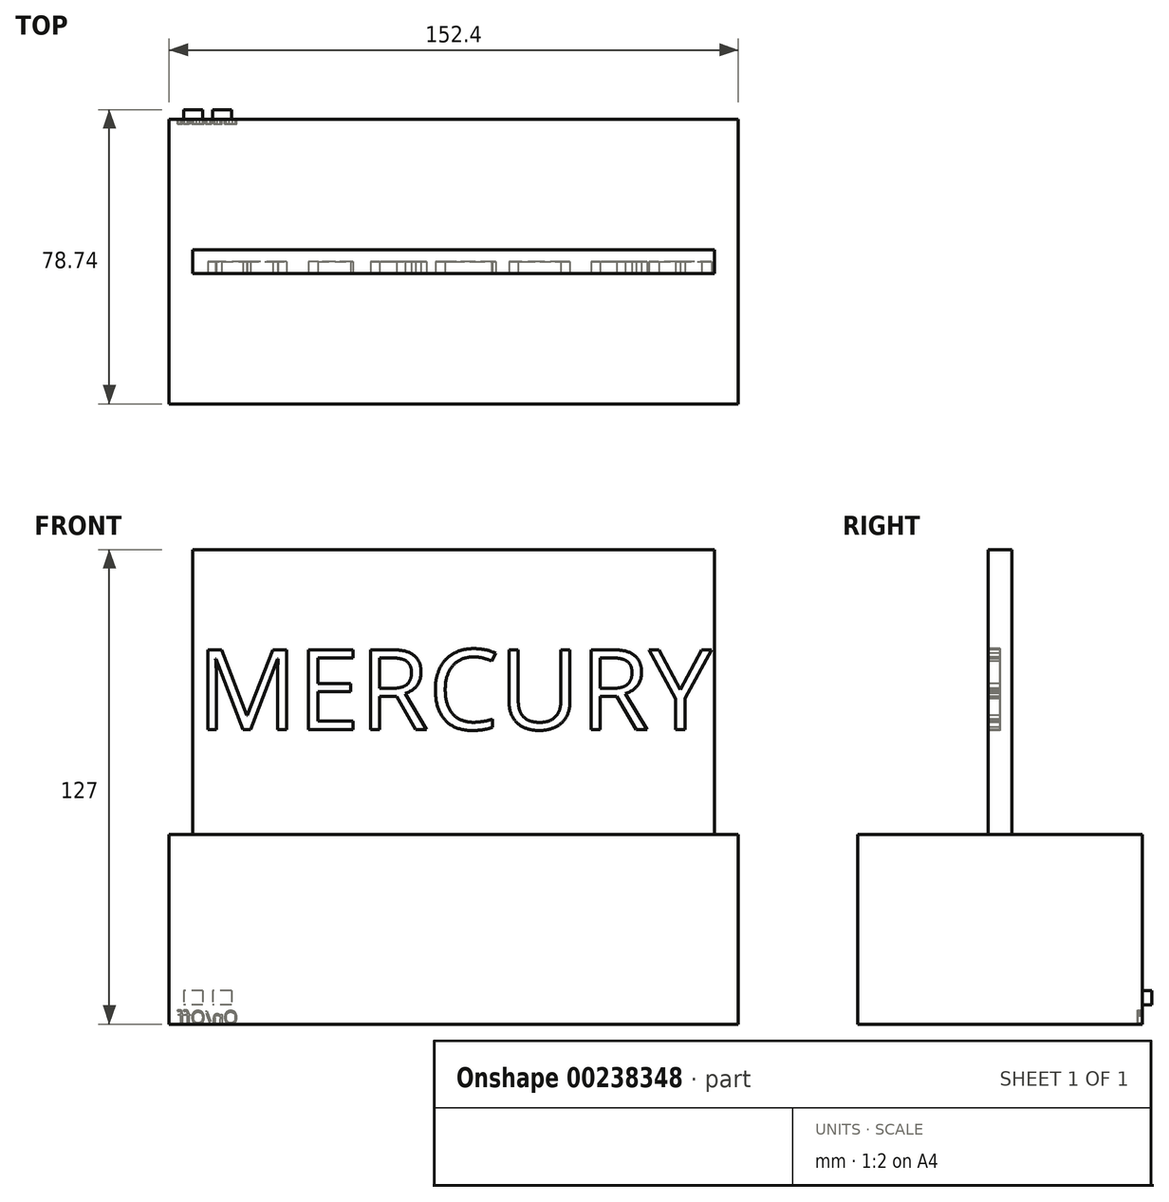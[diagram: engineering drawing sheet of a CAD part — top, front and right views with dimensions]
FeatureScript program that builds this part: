
annotation { "Feature Type Name" : "Feature", "Feature Type Description" : "" }
export const myFeature = defineFeature(function(context is Context, id is Id, definition is map)
    precondition{}
    {
        {
            var Q0;
            Q0=qCreatedBy(makeId("Top.planeOp"),FACE);
            var sketch = newSketch(context, id + "F0", { "sketchPlane" : qUnion([Q0])});
            skLineSegment(sketch, "E0.bottom", {"start": v(76.2, 38.1) * mm, "end": v(-76.2, 38.1) * mm});
            skLineSegment(sketch, "E0.top", {"start": v(76.2, -38.1) * mm, "end": v(-76.2, -38.1) * mm});
            skLineSegment(sketch, "E0.left", {"start": v(76.2, 38.1) * mm, "end": v(76.2, -38.1) * mm});
            skLineSegment(sketch, "E0.right", {"start": v(-76.2, 38.1) * mm, "end": v(-76.2, -38.1) * mm});
            skPoint(sketch, "E0.middle", {"position": v(0, 0) * mm});
            skSolve(sketch);
        }
        {
            var Q0;
            Q0=qSketchRegion(id+"F0",true);
            extrude(context, id + "F1", {"entities" : qUnion([Q0]), "depth" : 50.8 * mm});
        }
        {
            var Q0;
            Q0=makeQuery(id+"F1.opExtrude","CAP_FACE",FACE,{"disambiguationData":[OSD([sQuery(id+"F0.wireOp",EDGE,"E0.bottom"),sQuery(id+"F0.wireOp",EDGE,"E0.top"),sQuery(id+"F0.wireOp",EDGE,"E0.left"),sQuery(id+"F0.wireOp",EDGE,"E0.right")])],"isStart":false});
            var sketch = newSketch(context, id + "F2", { "sketchPlane" : qUnion([Q0])});
            skLineSegment(sketch, "E1.bottom", {"start": v(69.85, 3.18) * mm, "end": v(-69.85, 3.18) * mm});
            skLineSegment(sketch, "E1.top", {"start": v(69.85, -3.18) * mm, "end": v(-69.85, -3.18) * mm});
            skLineSegment(sketch, "E1.left", {"start": v(69.85, 3.18) * mm, "end": v(69.85, -3.18) * mm});
            skLineSegment(sketch, "E1.right", {"start": v(-69.85, 3.18) * mm, "end": v(-69.85, -3.18) * mm});
            skPoint(sketch, "E1.middle", {"position": v(0, 0) * mm});
            skSolve(sketch);
        }
        {
            var Q0;
            Q0=makeQuery(id+"F2.imprint","IMPRINT",FACE,{"disambiguationData":[TD([[makeQuery(id+"F2.imprint","IMPRINT",EDGE,{"derivedFrom":sQuery(id+"F2.wireOp",EDGE,"E1.bottom")}),1.0]])]});
            extrude(context, id + "F3", {"entities" : qUnion([Q0]), "operationType" : NewBodyOperationType.ADD, "depth" : 76.2 * mm});
        }
        {
            var Q0;
            Q0=makeQuery(id+"F1.opExtrude","SWEPT_FACE",FACE,{"disambiguationData":[OSD([sQuery(id+"F0.wireOp",EDGE,"E0.bottom")])]});
            var sketch = newSketch(context, id + "F4", { "sketchPlane" : qUnion([Q0])});
            skLineSegment(sketch, "E2.bottom", {"start": v(76.2, 0) * mm, "end": v(55.75, 0) * mm});
            skLineSegment(sketch, "E2.top", {"start": v(76.2, 9.14) * mm, "end": v(55.75, 9.14) * mm});
            skLineSegment(sketch, "E2.left", {"start": v(76.2, 0) * mm, "end": v(76.2, 9.14) * mm});
            skLineSegment(sketch, "E2.right", {"start": v(55.75, 0) * mm, "end": v(55.75, 9.14) * mm});
            skSolve(sketch);
        }
        {
            var Q0;
            Q0=makeQuery(id+"F3.opExtrude","SWEPT_FACE",FACE,{"disambiguationData":[OSD([sQuery(id+"F2.wireOp",EDGE,"E1.top")])]});
            var sketch = newSketch(context, id + "F5", { "sketchPlane" : qUnion([Q0])});
            skText(sketch, "E3", { "text": "MERCURY", "fontName": "OpenSans-Regular.ttf"});
            const initialGuessF5  = {"E3": [-0.06876, 0.07887, 1, 0, 0.0215]};
            skSetInitialGuess(sketch, initialGuessF5);
            skSolve(sketch);
        }
        {
            var Q0;
            Q0=qSketchRegion(id+"F5",true);
            extrude(context, id + "F6", {"entities" : qUnion([Q0]), "operationType" : NewBodyOperationType.REMOVE, "oppositeDirection" : true, "depth" : 3.17 * mm});
        }
        {
            var Q0;
            {var subQ2=sQuery(id+"F4.wireOp",EDGE,"E2.top");Q0=makeQuery(id+"F4.imprint","IMPRINT",FACE,{"disambiguationData":[TD([[makeQuery(id+"F4.imprint","IMPRINT",EDGE,{"derivedFrom":subQ2}),-1.0]])]});}
            var sketch = newSketch(context, id + "F7", { "sketchPlane" : qUnion([Q0])});
            skText(sketch, "E4", { "text": "On/Off", "fontName": "OpenSans-Regular.ttf"});
            const initialGuessF7  = {"E4": [0.05777, 0, 1, 0, 0.00358]};
            skSetInitialGuess(sketch, initialGuessF7);
            skSolve(sketch);
        }
        {
            var Q0;
            Q0 = qSketchRegion(id + "F7", true);
            extrude(context, id + "F8", {"entities" : qUnion([Q0]), "operationType" : NewBodyOperationType.REMOVE, "endBound" : BoundingType.SYMMETRIC, "oppositeDirection" : true, "depth" : 2.54 * mm});
        }
        {
            var Q0;
            Q0=makeQuery(id+"F4.imprint","IMPRINT",FACE,{"disambiguationData":[TD([[makeQuery(id+"F4.imprint","IMPRINT",EDGE,{"derivedFrom":sQuery(id+"F4.wireOp",EDGE,"E2.bottom")}),1.0]])]});
            var sketch = newSketch(context, id + "F9", { "sketchPlane" : qUnion([Q0])});
            skLineSegment(sketch, "E5.bottom", {"start": v(59.52, 8.93) * mm, "end": v(64.6, 8.93) * mm});
            skLineSegment(sketch, "E5.top", {"start": v(59.52, 5.12) * mm, "end": v(64.6, 5.12) * mm});
            skLineSegment(sketch, "E5.left", {"start": v(59.52, 8.93) * mm, "end": v(59.52, 5.12) * mm});
            skLineSegment(sketch, "E5.right", {"start": v(64.6, 8.93) * mm, "end": v(64.6, 5.12) * mm});
            skLineSegment(sketch, "E6.bottom", {"start": v(67.2, 8.92) * mm, "end": v(72.27, 8.92) * mm});
            skLineSegment(sketch, "E6.top", {"start": v(67.2, 5.11) * mm, "end": v(72.27, 5.11) * mm});
            skLineSegment(sketch, "E6.left", {"start": v(67.2, 8.92) * mm, "end": v(67.2, 5.11) * mm});
            skLineSegment(sketch, "E6.right", {"start": v(72.27, 8.92) * mm, "end": v(72.27, 5.11) * mm});
            skSolve(sketch);
        }
        {
            var Q0;
            Q0 = qSketchRegion(id + "F9", true);
            extrude(context, id + "F10", {"entities" : qUnion([Q0]), "operationType" : NewBodyOperationType.ADD, "depth" : 2.54 * mm});
        }
    });
